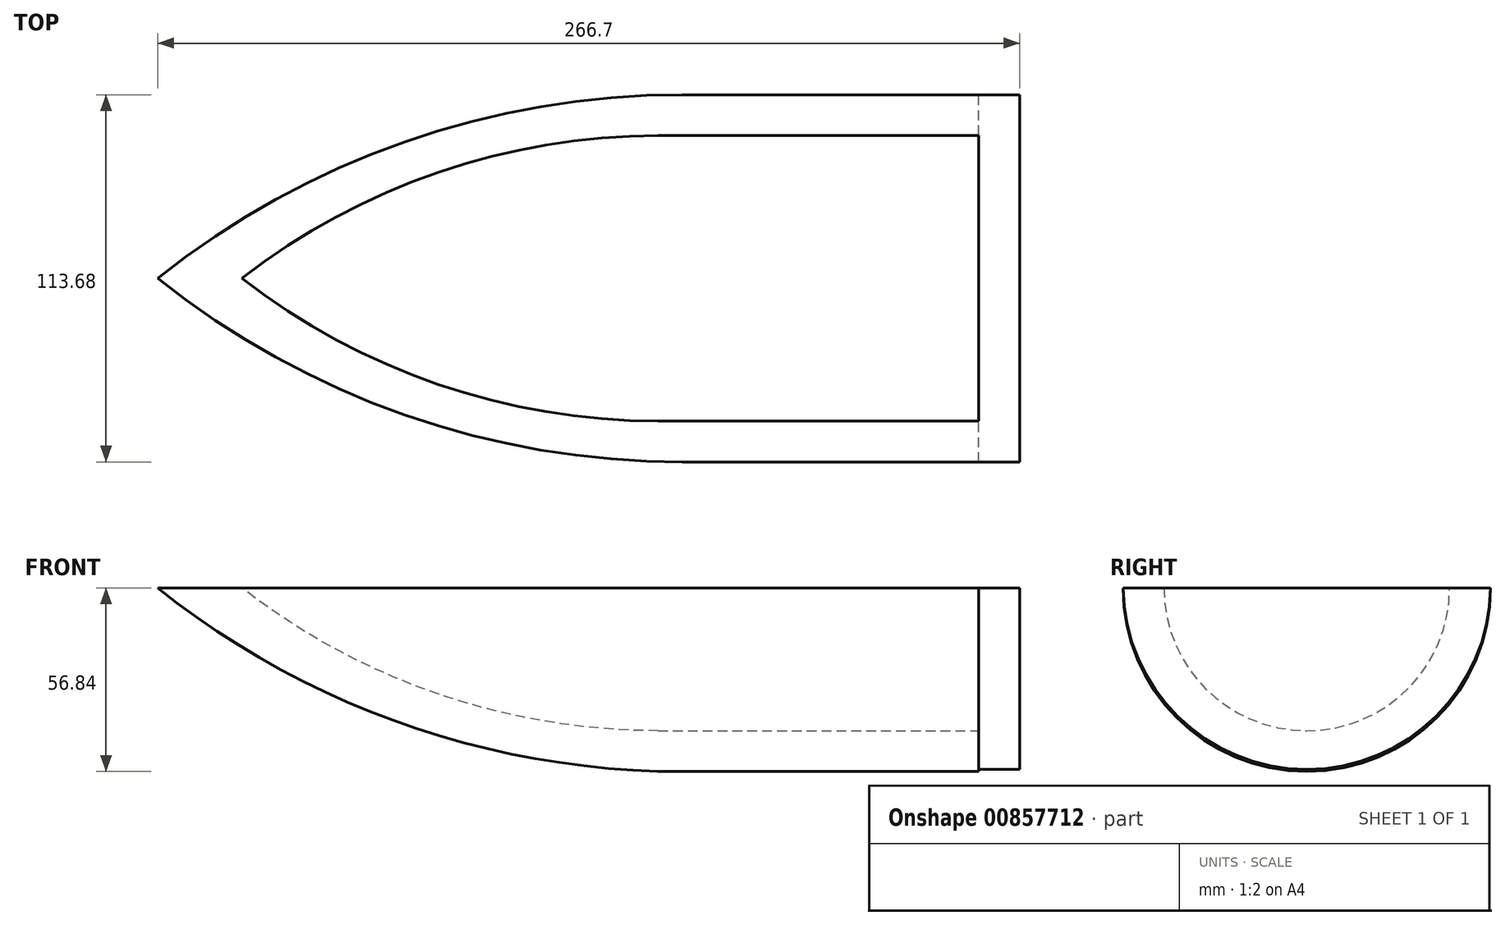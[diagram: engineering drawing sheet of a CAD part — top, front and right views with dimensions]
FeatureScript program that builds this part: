
annotation { "Feature Type Name" : "Feature", "Feature Type Description" : "" }
export const myFeature = defineFeature(function(context is Context, id is Id, definition is map)
    precondition{}
    {
        {
            var Q0;
            Q0=qCreatedBy(makeId("Front.planeOp"),FACE);
            var sketch = newSketch(context, id + "F0", { "sketchPlane" : qUnion([Q0])});
            skLineSegment(sketch, "E0.bottom", {"start": v(91.7, 56.84) * mm, "end": v(0, 56.84) * mm});
            skLineSegment(sketch, "E0.top", {"start": v(91.7, 0) * mm, "end": v(0, 0) * mm});
            skLineSegment(sketch, "E0.left", {"start": v(91.7, 56.84) * mm, "end": v(91.7, 0) * mm});
            skLineSegment(sketch, "E0.right", {"start": v(0, 56.84) * mm, "end": v(0, 0) * mm});
            skLineSegment(sketch, "E1", {"start": v(0, 56.84) * mm, "end": v(-162.3, 56.84) * mm});
            skArc(sketch, "E2", {"start": v(-162.3, 56.84) * mm, "mid": v(-85.99, 14.62) * mm, "end": v(0, 0) * mm});
            skLineSegment(sketch, "E3", {"start": v(91.7, 12.66) * mm, "end": v(-7.46, 12.66) * mm});
            skArc(sketch, "E4", {"start": v(-136.23, 56.84) * mm, "mid": v(-75.53, 24) * mm, "end": v(-7.46, 12.66) * mm});
            skSolve(sketch);
        }
        {
            var Q0;
            {var subQ0=sQuery(id+"F0.wireOp",EDGE,"E2");Q0=makeQuery(id+"F0.imprint","IMPRINT",FACE,{"disambiguationData":[TD([[makeQuery(id+"F0.imprint","IMPRINT",EDGE,{"derivedFrom":subQ0}),1.0]])]});}
            var Q1;
            {var subQ0=sQuery(id+"F0.wireOp",EDGE,"E0.top");Q1=makeQuery(id+"F0.imprint","IMPRINT",FACE,{"disambiguationData":[TD([[makeQuery(id+"F0.imprint","IMPRINT",EDGE,{"derivedFrom":subQ0}),-1.0]])]});}
            var Q2;
            Q2=sQuery(id+"F0.wireOp",EDGE,"E1");
            revolve(context, id + "F1", {"surfaceOperationType" : NewSurfaceOperationType.NEW, "entities" : qUnion([Q0, Q1]), "axis" : qUnion([Q2]), "revolveType" : RevolveType.SYMMETRIC, "angle" : 180 * degree});
        }
        {
            var Q0;
            Q0=makeQuery(id+"F1.opRevolve","SWEPT_FACE",FACE,{"disambiguationData":[OSD([sQuery(id+"F0.wireOp",EDGE,"E0.left")])]});
            var sketch = newSketch(context, id + "F2", { "sketchPlane" : qUnion([Q0])});
            skArc(sketch, "E5", {"start": v(-56.84, 56.84) * mm, "mid": v(0, 0.7) * mm, "end": v(56.84, 56.84) * mm});
            skLineSegment(sketch, "E6", {"start": v(-56.84, 56.84) * mm, "end": v(56.84, 56.84) * mm});
            skSolve(sketch);
        }
        {
            var Q0;
            Q0 = qSketchRegion(id + "F2", true);
            extrude(context, id + "F3", {"entities" : qUnion([Q0]), "operationType" : NewBodyOperationType.ADD, "depth" : 12.7 * mm, "offsetDistance" : 25.4 * mm});
        }
    });
